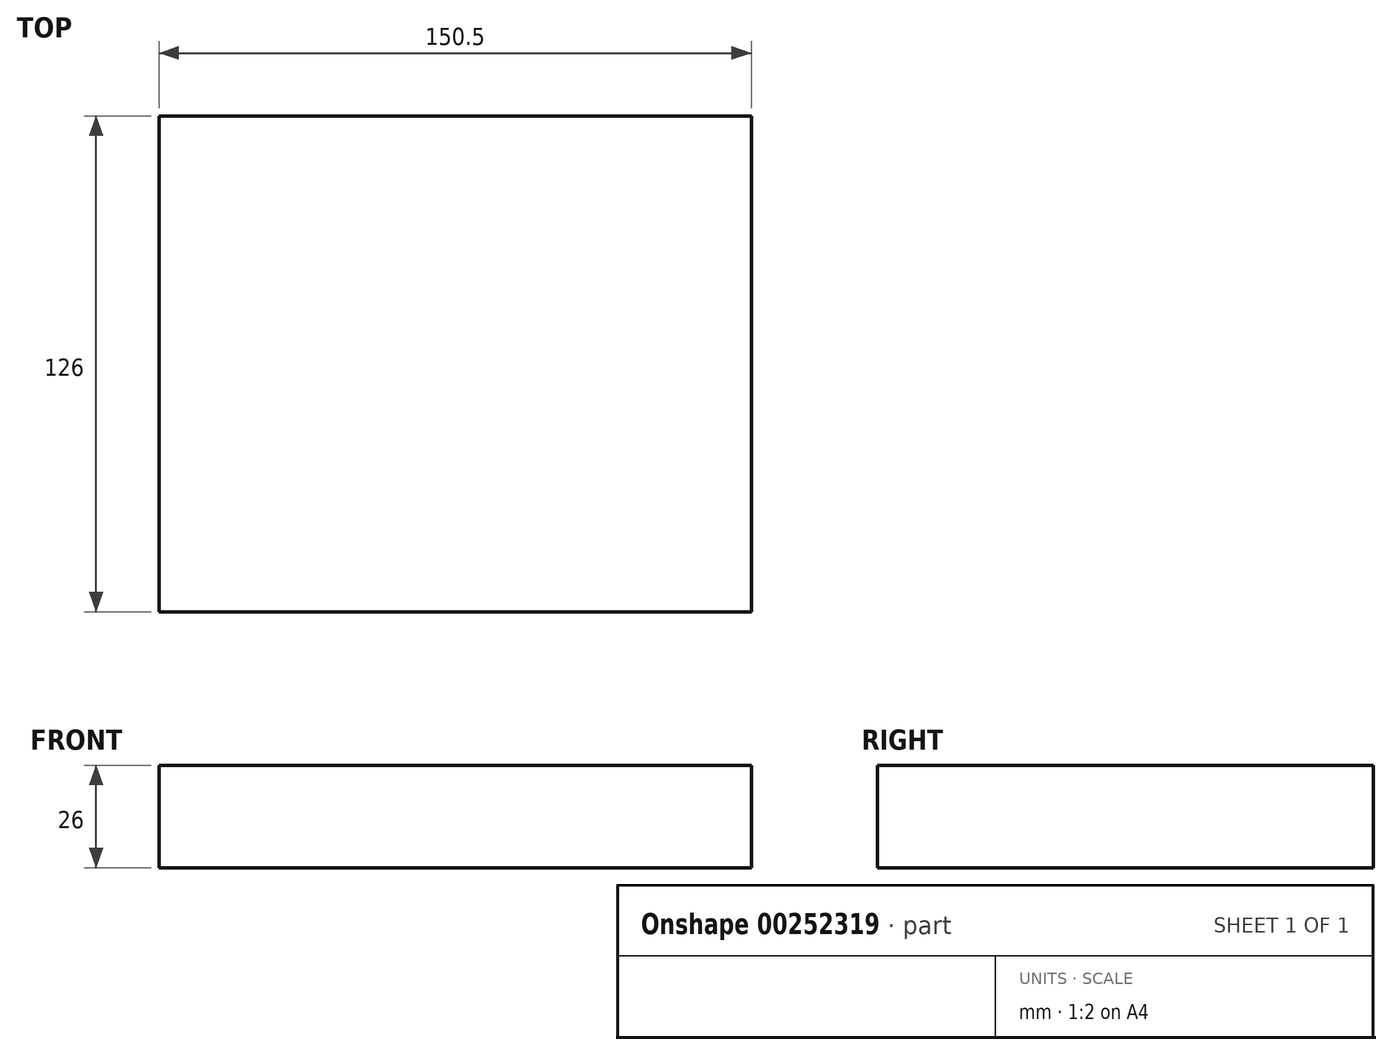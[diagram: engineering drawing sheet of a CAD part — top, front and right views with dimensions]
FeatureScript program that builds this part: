
annotation { "Feature Type Name" : "Feature", "Feature Type Description" : "" }
export const myFeature = defineFeature(function(context is Context, id is Id, definition is map)
    precondition{}
    {
        {
            var Q0;
            Q0=qCreatedBy(makeId("Front.planeOp"),FACE);
            var sketch = newSketch(context, id + "F0", { "sketchPlane" : qUnion([Q0])});
            skLineSegment(sketch, "E0.bottom", {"start": v(-75.25, 13) * mm, "end": v(75.25, 13) * mm});
            skLineSegment(sketch, "E0.top", {"start": v(-75.25, -13) * mm, "end": v(75.25, -13) * mm});
            skLineSegment(sketch, "E0.left", {"start": v(-75.25, 13) * mm, "end": v(-75.25, -13) * mm});
            skLineSegment(sketch, "E0.right", {"start": v(75.25, 13) * mm, "end": v(75.25, -13) * mm});
            skPoint(sketch, "E0.middle", {"position": v(0, 0) * mm});
            skSolve(sketch);
        }
        {
            var Q0;
            Q0=makeQuery(id+"F0.imprint","IMPRINT",FACE,{"disambiguationData":[TD([[makeQuery(id+"F0.imprint","IMPRINT",EDGE,{"derivedFrom":sQuery(id+"F0.wireOp",EDGE,"E0.bottom")}),-1.0]])]});
            extrude(context, id + "F1", {"entities" : qUnion([Q0]), "depth" : 126 * mm});
        }
    });
